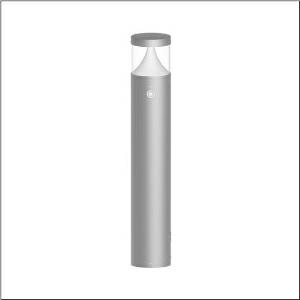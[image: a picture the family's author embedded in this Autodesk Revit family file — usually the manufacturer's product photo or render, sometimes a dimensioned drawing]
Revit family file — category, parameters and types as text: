
# Revit family: cl_31_poller_90_sensor_5cl444803
name_source: partatom
category: Lighting Fixtures
units: mm (PartAtom-declared; Revit-internal decimal feet)

## family parameters
Cut with Voids When Loaded = No
Host = Face
Light Source = No
Part Type = Normal
Room Calculation Point = No
Round Connector Dimension = Use Diameter
Shared = No

## types (1)
- --- (1 x LED, 1500 lm, 14 W, 3000K)
    Apparent Load = 14 VA
    CIE Flux Codes = 19 66 88 92 100
    Color Rendering = 80
    Color Temperature = 3000K
    Default Elevation = 1800 mm
    Description = CL 31 Bollard 90 Sensor, bollard luminaire, primary light control with lens, of PC, primary optical cover: cover panel, of PC, transparent, secondary light control with reflector, of PC, primary light characteristic: asymmetric, LED, rated luminous flux: 1.500lm, luminous efficacy: 107lm/W, light colour: 830, colour temperature: 3000K, control gear: DALI, with terminal, 5-pole, max. 2.5mm², mains connection: 220..240V, AC, 50/60Hz, rated input power: 14W, luminaire housing, of aluminium, powder-coated, Siteco® metallic grey, diameter: 170mm, height: 900mm, PIR sensor, protection rating (complete): IP65, insulation class (complete): insulation class I (protective earthing), certification: CE, ENEC, impact resistance: IK08, permissible operating ambient temperature for outdoor applications: -20..+50°C, packaging unit: 1 piece
    Height = 200 mm  [stored 0.656168 ft]
    Lamp = 1 x LED
    Lamp Light Flux = 1500 lm
    Lamp Power = 14 W
    Lamp count = 1
    Length = 170 mm  [stored 0.557743 ft]
    Luminous efficacy = 107 lm/W
    Manufacturer = Siteco
    ModVariant = No
    Model = 5CL444803
    Mounting Place = Floor
    Mounting Type = Freestanding
    Number of Poles = 1
    OnlyDefault = Yes
    Power Factor = 1
    Product Name = CL 31 Poller 90 Sensor
    Product group = bollard luminaire
    ProductGroupID = 1304
    Protection Class = Protection class I
    Protection Degree = IP 65
    RLX_Detail_Level = 1
    RLX_Emergency_Light_Flux = 0 lm
    RLX_Emergency_Type = 0
    RLX_Emergency_Type_DB = No
    RlxData = <blob elided: 65089 chars, md5=23de825d>
    Socket = socket
    Standby Power = 0 W
    System Light Flux = 1500 lm
    System Power = 14 W
    Type Comments = factory setting: luminous flux: 100 % | dim-lin: 254 | 350 mA
    Type Image = l_1006897.jpg
    URL = http://relux.com
    VarID = @adj_216425
    Voltage = 0 V
    Weight = 0.00 kg
    Width = 0 mm  [stored 0 ft]

note: [stored X ft] marks values corroborated as IEEE doubles in the binary element streams (Revit-internal decimal feet)

## geometry (parser evidence)
native form markers: Blend x4, Sweep x9
no freeform markers — native parametric forms only
